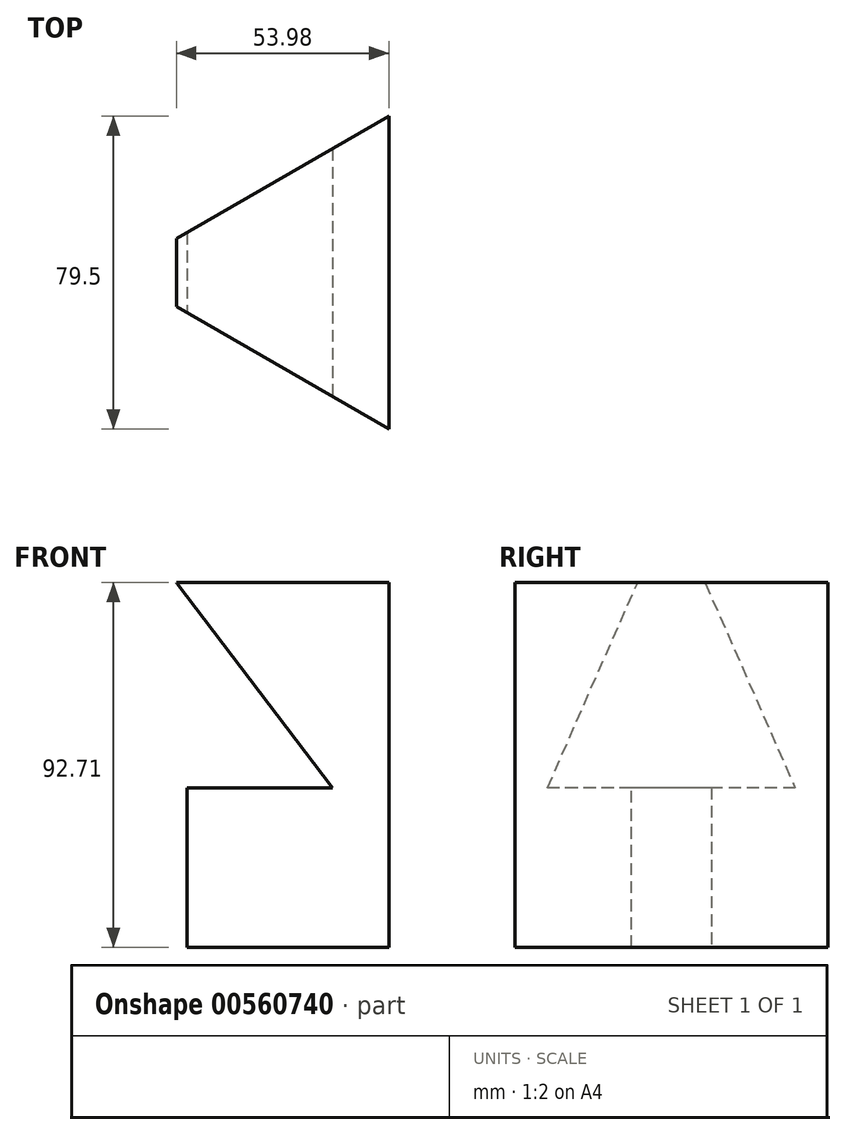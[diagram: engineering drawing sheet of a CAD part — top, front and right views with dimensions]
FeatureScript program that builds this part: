
annotation { "Feature Type Name" : "Feature", "Feature Type Description" : "" }
export const myFeature = defineFeature(function(context is Context, id is Id, definition is map)
    precondition{}
    {
        {
            var Q0;
            Q0=qCreatedBy(makeId("Top.planeOp"),FACE);
            var sketch = newSketch(context, id + "F0", { "sketchPlane" : qUnion([Q0])});
            skCircle(sketch, "E0.cCircle", {"center": v(0, 0) * mm, "radius": 22.95 * mm, "construction": true});
            skLineSegment(sketch, "E0.0", {"start": v(22.95, 39.75) * mm, "end": v(22.95, -39.75) * mm});
            skLineSegment(sketch, "E0.1", {"start": v(22.95, -39.75) * mm, "end": v(-45.9, 0) * mm});
            skLineSegment(sketch, "E0.2", {"start": v(-45.9, 0) * mm, "end": v(22.95, 39.75) * mm});
            skPoint(sketch, "E0.0.midPoint", {"position": v(22.95, 0) * mm});
            skSolve(sketch);
        }
        {
            var Q0;
            Q0 = qSketchRegion(id + "F0", true);
            extrude(context, id + "F1", {"entities" : qUnion([Q0]), "depth" : 92.7 * mm, "offsetDistance" : 25.4 * mm});
        }
        {
            var Q0;
            Q0=qCreatedBy(makeId("Front.planeOp"),FACE);
            cPlane(context, id + "F2", {"entities" : qUnion([Q0]), "cplaneType" : CPlaneType.OFFSET, "offset" : 254 * mm, "width" : 152.4 * mm, "height" : 152.4 * mm});
        }
        {
            var Q0;
            Q0=qCreatedBy(id+"F2.planeOp",FACE);
            var sketch = newSketch(context, id + "F3", { "sketchPlane" : qUnion([Q0])});
            skLineSegment(sketch, "E1", {"start": v(-61.28, 0) * mm, "end": v(-28.3, 0) * mm});
            skLineSegment(sketch, "E2", {"start": v(-28.3, 0) * mm, "end": v(-28.3, 40.58) * mm});
            skLineSegment(sketch, "E3", {"start": v(-28.3, 40.58) * mm, "end": v(8.57, 40.58) * mm});
            skLineSegment(sketch, "E4", {"start": v(8.57, 40.58) * mm, "end": v(-30.9, 92.52) * mm});
            skLineSegment(sketch, "E5", {"start": v(-30.9, 92.52) * mm, "end": v(-33.76, 96.67) * mm});
            skLineSegment(sketch, "E6", {"start": v(-33.76, 96.67) * mm, "end": v(-61.28, 96.67) * mm});
            skLineSegment(sketch, "E7", {"start": v(-61.28, 96.67) * mm, "end": v(-61.28, 0) * mm});
            skSolve(sketch);
        }
        {
            var Q0;
            Q0=makeQuery(id+"F3.imprint","IMPRINT",FACE,{"disambiguationData":[TD([[makeQuery(id+"F3.imprint","IMPRINT",EDGE,{"derivedFrom":sQuery(id+"F3.wireOp",EDGE,"E1")}),1.0]])]});
            extrude(context, id + "F4", {"entities" : qUnion([Q0]), "operationType" : NewBodyOperationType.REMOVE, "oppositeDirection" : true, "depth" : 539.24 * mm, "offsetDistance" : 25.4 * mm});
        }
    });
